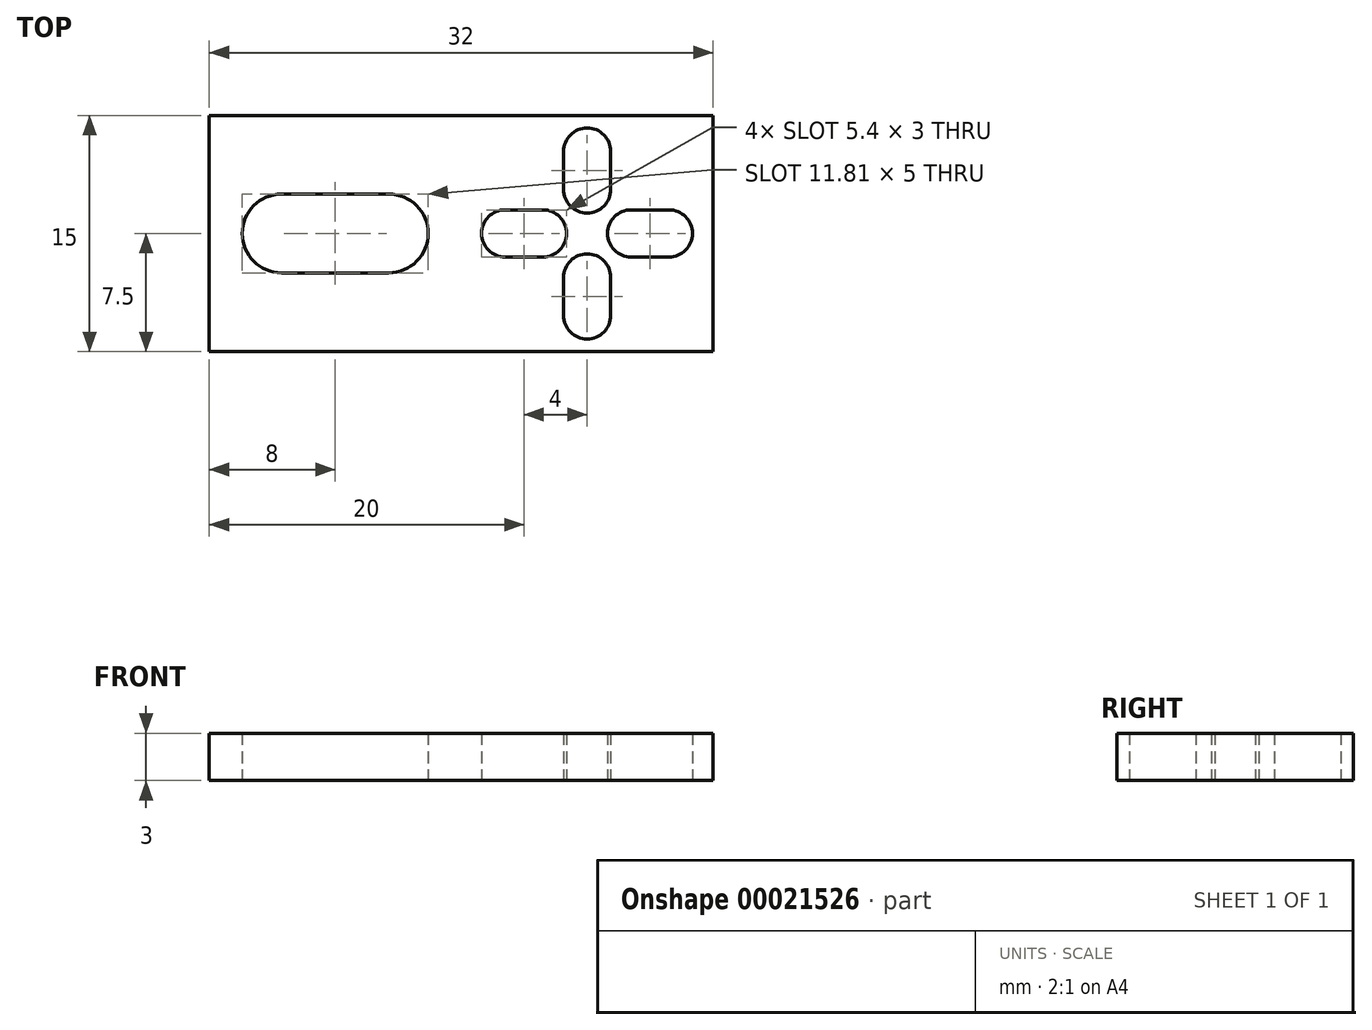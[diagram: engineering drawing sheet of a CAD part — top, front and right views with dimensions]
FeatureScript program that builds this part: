
annotation { "Feature Type Name" : "Feature", "Feature Type Description" : "" }
export const myFeature = defineFeature(function(context is Context, id is Id, definition is map)
    precondition{}
    {
        {
            var Q0;
            Q0=qCreatedBy(makeId("Top.planeOp"),FACE);
            var sketch = newSketch(context, id + "F0", { "sketchPlane" : qUnion([Q0])});
            skLineSegment(sketch, "E0.rect.bottom", {"start": v(16, -7.5) * mm, "end": v(-16, -7.5) * mm});
            skLineSegment(sketch, "E0.rect.top", {"start": v(16, 7.5) * mm, "end": v(-16, 7.5) * mm});
            skLineSegment(sketch, "E0.rect.left", {"start": v(16, -7.5) * mm, "end": v(16, 7.5) * mm});
            skLineSegment(sketch, "E0.rect.right", {"start": v(-16, -7.5) * mm, "end": v(-16, 7.5) * mm});
            skPoint(sketch, "E0.rect.middle", {"position": v(0, 0) * mm});
            skArc(sketch, "E1", {"start": v(-4.6, -2.5) * mm, "mid": v(-2.1, 0) * mm, "end": v(-4.6, 2.5) * mm});
            skArc(sketch, "E2", {"start": v(-11.4, 2.5) * mm, "mid": v(-13.9, 0) * mm, "end": v(-11.4, -2.5) * mm});
            skLineSegment(sketch, "E3", {"start": v(-11.4, 2.5) * mm, "end": v(-4.6, 2.5) * mm});
            skLineSegment(sketch, "E4", {"start": v(-11.4, -2.5) * mm, "end": v(-4.6, -2.5) * mm});
            skArc(sketch, "E5", {"start": v(2.8, 1.5) * mm, "mid": v(1.3, 0) * mm, "end": v(2.8, -1.5) * mm});
            skArc(sketch, "E6", {"start": v(5.2, -1.5) * mm, "mid": v(6.7, 0) * mm, "end": v(5.2, 1.5) * mm});
            skLineSegment(sketch, "E7", {"start": v(2.8, 1.5) * mm, "end": v(5.2, 1.5) * mm});
            skLineSegment(sketch, "E8", {"start": v(2.8, -1.5) * mm, "end": v(5.2, -1.5) * mm});
            skArc(sketch, "E9.1.0", {"start": v(6.5, -5.2) * mm, "mid": v(8, -6.7) * mm, "end": v(9.5, -5.2) * mm});
            skLineSegment(sketch, "E9.1.1", {"start": v(6.5, -5.2) * mm, "end": v(6.5, -2.8) * mm});
            skArc(sketch, "E9.1.2", {"start": v(9.5, -2.8) * mm, "mid": v(8, -1.3) * mm, "end": v(6.5, -2.8) * mm});
            skLineSegment(sketch, "E9.1.3", {"start": v(9.5, -5.2) * mm, "end": v(9.5, -2.8) * mm});
            skArc(sketch, "E9.2.0", {"start": v(13.2, -1.5) * mm, "mid": v(14.7, 0) * mm, "end": v(13.2, 1.5) * mm});
            skLineSegment(sketch, "E9.2.1", {"start": v(13.2, -1.5) * mm, "end": v(10.8, -1.5) * mm});
            skArc(sketch, "E9.2.2", {"start": v(10.8, 1.5) * mm, "mid": v(9.3, 0) * mm, "end": v(10.8, -1.5) * mm});
            skLineSegment(sketch, "E9.2.3", {"start": v(13.2, 1.5) * mm, "end": v(10.8, 1.5) * mm});
            skArc(sketch, "E9.3.0", {"start": v(9.5, 5.2) * mm, "mid": v(8, 6.7) * mm, "end": v(6.5, 5.2) * mm});
            skLineSegment(sketch, "E9.3.1", {"start": v(9.5, 5.2) * mm, "end": v(9.5, 2.8) * mm});
            skArc(sketch, "E9.3.2", {"start": v(6.5, 2.8) * mm, "mid": v(8, 1.3) * mm, "end": v(9.5, 2.8) * mm});
            skLineSegment(sketch, "E9.3.3", {"start": v(6.5, 5.2) * mm, "end": v(6.5, 2.8) * mm});
            skPoint(sketch, "E9.center", {"position": v(8, 0) * mm});
            skLineSegment(sketch, "E10", {"start": v(0, 0) * mm, "end": v(16, 0) * mm});
            skSolve(sketch);
        }
        {
            var Q0;
            {var subQ6=sQuery(id+"F0.wireOp",EDGE,"E0.rect.bottom");Q0=makeQuery(id+"F0.imprint","IMPRINT",FACE,{"disambiguationData":[TD([[makeQuery(id+"F0.imprint","IMPRINT",EDGE,{"derivedFrom":subQ6}),-1.0]])]});}
            extrude(context, id + "F1", {"entities" : qUnion([Q0]), "depth" : 3 * mm});
        }
    });
